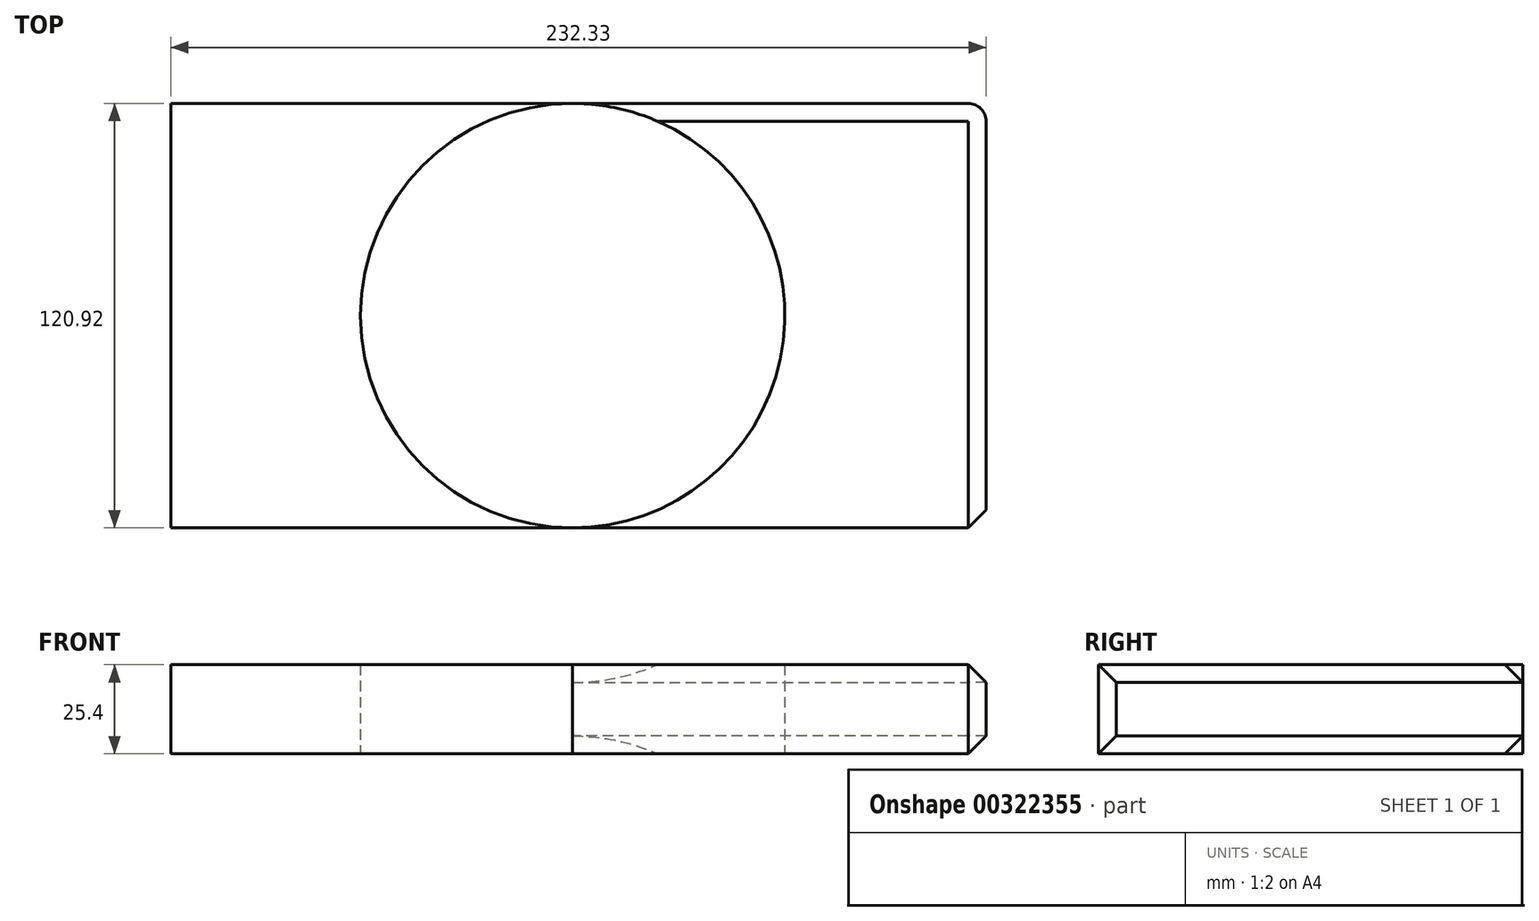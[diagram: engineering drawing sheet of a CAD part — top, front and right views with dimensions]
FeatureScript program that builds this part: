
annotation { "Feature Type Name" : "Feature", "Feature Type Description" : "" }
export const myFeature = defineFeature(function(context is Context, id is Id, definition is map)
    precondition{}
    {
        {
            var Q0;
            Q0=qCreatedBy(makeId("Top.planeOp"),FACE);
            var sketch = newSketch(context, id + "F0", { "sketchPlane" : qUnion([Q0])});
            skLineSegment(sketch, "E0.bottom", {"start": v(-129.63, -66.95) * mm, "end": v(-114.5, -66.95) * mm});
            skLineSegment(sketch, "E0.top", {"start": v(-129.63, -60.46) * mm, "end": v(-114.5, -60.46) * mm});
            skLineSegment(sketch, "E0.left", {"start": v(-129.63, -66.95) * mm, "end": v(-129.63, -60.46) * mm});
            skLineSegment(sketch, "E0.right", {"start": v(-114.5, -66.95) * mm, "end": v(-114.5, -60.46) * mm});
            skLineSegment(sketch, "E1.bottom", {"start": v(-114.5, -60.46) * mm, "end": v(117.83, -60.46) * mm});
            skLineSegment(sketch, "E1.top", {"start": v(-114.5, 60.46) * mm, "end": v(117.83, 60.46) * mm});
            skLineSegment(sketch, "E1.left", {"start": v(-114.5, -60.46) * mm, "end": v(-114.5, 60.46) * mm});
            skLineSegment(sketch, "E1.right", {"start": v(117.83, -60.46) * mm, "end": v(117.83, 60.46) * mm});
            skCircle(sketch, "E2", {"center": v(0, 0) * mm, "radius": 60.46 * mm});
            skSolve(sketch);
        }
        {
            var Q0;
            {var subQ0=sQuery(id+"F0.wireOp",EDGE,"E1.right");Q0=makeQuery(id+"F0.imprint","IMPRINT",FACE,{"disambiguationData":[TD([[makeQuery(id+"F0.imprint","IMPRINT",EDGE,{"derivedFrom":subQ0}),1.0]])]});}
            var Q1;
            {var subQ0=sQuery(id+"F0.wireOp",EDGE,"E1.left");Q1=makeQuery(id+"F0.imprint","IMPRINT",FACE,{"disambiguationData":[TD([[makeQuery(id+"F0.imprint","IMPRINT",EDGE,{"derivedFrom":subQ0}),-1.0]])]});}
            extrude(context, id + "F1", {"entities" : qUnion([Q0, Q1]), "depth" : 25.4 * mm});
        }
        {
            var Q0;
            Q0=makeQuery(id+"F1.opExtrude","SWEPT_EDGE",EDGE,{"disambiguationData":[OSD([sQuery(id+"F0.wireOp",EDGE,"E1.top"),sQuery(id+"F0.wireOp",EDGE,"E1.right")])]});
            fillet(context, id + "F2", {"entities" : qUnion([Q0]), "radius" : 5.08 * mm, "tangentPropagation" : true, "allowEdgeOverflow" : false});
        }
        {
            var Q0;
            Q0=makeQuery(id+"F1.opExtrude","SWEPT_FACE",FACE,{"disambiguationData":[OSD([sQuery(id+"F0.wireOp",EDGE,"E1.right")])]});
            chamfer(context, id + "F3", {"entities" : qUnion([Q0]), "width" : 5.08 * mm, "tangentPropagation" : true});
        }
    });
